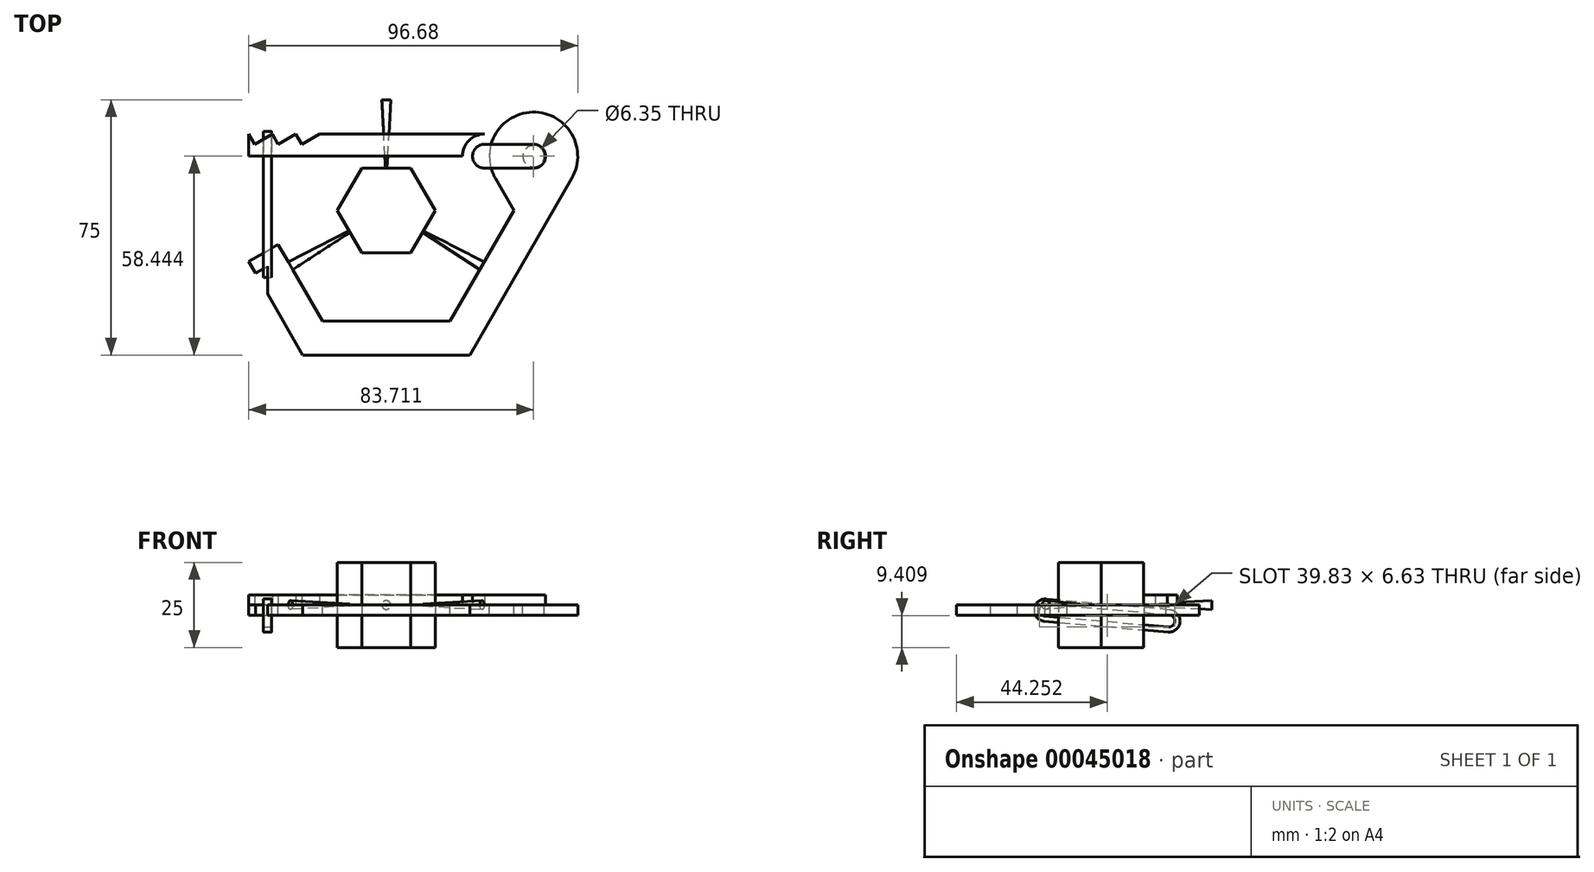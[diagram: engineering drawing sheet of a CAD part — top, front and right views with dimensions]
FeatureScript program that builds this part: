
annotation { "Feature Type Name" : "Feature", "Feature Type Description" : "" }
export const myFeature = defineFeature(function(context is Context, id is Id, definition is map)
    precondition{}
    {
        {
            var Q0;
            Q0=qCreatedBy(makeId("Top.planeOp"),FACE);
            var sketch = newSketch(context, id + "F0", { "sketchPlane" : qUnion([Q0])});
            skCircle(sketch, "E0.cCircle", {"center": v(0, 0) * mm, "radius": 12.5 * mm, "construction": true});
            skLineSegment(sketch, "E0.0", {"start": v(7.22, 12.5) * mm, "end": v(14.43, 0) * mm});
            skLineSegment(sketch, "E0.1", {"start": v(14.43, 0) * mm, "end": v(7.22, -12.5) * mm});
            skLineSegment(sketch, "E0.2", {"start": v(7.22, -12.5) * mm, "end": v(-7.22, -12.5) * mm});
            skLineSegment(sketch, "E0.3", {"start": v(-7.22, -12.5) * mm, "end": v(-14.43, 0) * mm});
            skLineSegment(sketch, "E0.4", {"start": v(-14.43, 0) * mm, "end": v(-7.22, 12.5) * mm});
            skLineSegment(sketch, "E0.5", {"start": v(-7.22, 12.5) * mm, "end": v(7.22, 12.5) * mm});
            skLineSegment(sketch, "E1.0", {"start": v(32.07, 9.46) * mm, "end": v(37.53, 0) * mm});
            skLineSegment(sketch, "E1.1", {"start": v(18.76, -32.5) * mm, "end": v(-18.76, -32.5) * mm});
            skLineSegment(sketch, "E1.2", {"start": v(-18.76, -32.5) * mm, "end": v(-31.75, -10) * mm});
            skLineSegment(sketch, "E1.3", {"start": v(37.53, 0) * mm, "end": v(18.76, -32.5) * mm});
            skLineSegment(sketch, "E2.0", {"start": v(-24.54, -42.5) * mm, "end": v(-40.41, -15) * mm});
            skLineSegment(sketch, "E2.1", {"start": v(24.54, -42.5) * mm, "end": v(-24.54, -42.5) * mm});
            skLineSegment(sketch, "E2.2", {"start": v(49.07, 0) * mm, "end": v(24.54, -42.5) * mm});
            skLineSegment(sketch, "E3", {"start": v(-40.41, -15) * mm, "end": v(-31.75, -10) * mm});
            skLineSegment(sketch, "E4", {"start": v(49.07, 0) * mm, "end": v(54.54, 9.46) * mm});
            skCircle(sketch, "E5", {"center": v(43.3, 15.94) * mm, "radius": 3.18 * mm});
            skLineSegment(sketch, "E6", {"start": v(-31.75, -10) * mm, "end": v(24.54, 22.5) * mm, "construction": true});
            skArc(sketch, "E7", {"start": v(32.07, 9.46) * mm, "mid": v(43.3, 28.92) * mm, "end": v(54.54, 9.46) * mm});
            skPoint(sketch, "E8.start.orphan", {"position": v(43.3, 33.33) * mm});
            skPoint(sketch, "E9.orphan", {"position": v(62.07, 22.5) * mm});
            skLineSegment(sketch, "E10", {"start": v(-38.41, -18.47) * mm, "end": v(-34.9, -16.44) * mm});
            skLineSegment(sketch, "E11", {"start": v(-34.9, -16.44) * mm, "end": v(-34.9, -24.55) * mm});
            skSolve(sketch);
        }
        {
            var Q0;
            Q0=qCreatedBy(makeId("Top.planeOp"),FACE);
            var sketch = newSketch(context, id + "F1", { "sketchPlane" : qUnion([Q0])});
            skLineSegment(sketch, "E12", {"start": v(43.3, 15.94) * mm, "end": v(28.87, 15.94) * mm, "construction": true});
            skArc(sketch, "E13.0.startCap", {"start": v(43.3, 19.44) * mm, "mid": v(46.8, 15.94) * mm, "end": v(43.3, 12.44) * mm});
            skArc(sketch, "E13.0.endCap", {"start": v(28.87, 12.44) * mm, "mid": v(25.37, 15.94) * mm, "end": v(28.87, 19.44) * mm});
            skLineSegment(sketch, "E13.0.left", {"start": v(43.3, 12.44) * mm, "end": v(28.87, 12.44) * mm});
            skLineSegment(sketch, "E13.0.right", {"start": v(43.3, 19.44) * mm, "end": v(28.87, 19.44) * mm});
            skLineSegment(sketch, "E14.0", {"start": v(37.82, 9.44) * mm, "end": v(28.87, 9.44) * mm});
            skLineSegment(sketch, "E14.2", {"start": v(37.82, 22.44) * mm, "end": v(28.87, 22.44) * mm});
            skArc(sketch, "E14.3", {"start": v(28.87, 9.44) * mm, "mid": v(22.37, 15.94) * mm, "end": v(28.87, 22.44) * mm});
            skLineSegment(sketch, "E15", {"start": v(28.87, 22.44) * mm, "end": v(-19.63, 22.44) * mm});
            skPoint(sketch, "E16.endSnap0", {"position": v(22.37, 15.94) * mm});
            skLineSegment(sketch, "E17", {"start": v(-40.41, 15.94) * mm, "end": v(22.37, 15.94) * mm});
            skArc(sketch, "E18", {"start": v(37.82, 22.44) * mm, "mid": v(51.8, 15.94) * mm, "end": v(37.82, 9.44) * mm});
            skLineSegment(sketch, "E19", {"start": v(-24.83, 19.44) * mm, "end": v(-19.63, 22.44) * mm});
            skLineSegment(sketch, "E20", {"start": v(-26.56, 22.44) * mm, "end": v(-24.83, 19.44) * mm});
            skLineSegment(sketch, "E21", {"start": v(-31.75, 19.44) * mm, "end": v(-26.56, 22.44) * mm});
            skLineSegment(sketch, "E22", {"start": v(-33.49, 22.44) * mm, "end": v(-31.75, 19.44) * mm});
            skLineSegment(sketch, "E23", {"start": v(-38.68, 19.44) * mm, "end": v(-33.49, 22.44) * mm});
            skLineSegment(sketch, "E24", {"start": v(-40.41, 22.44) * mm, "end": v(-38.68, 19.44) * mm});
            skLineSegment(sketch, "E25", {"start": v(-40.41, 22.44) * mm, "end": v(-40.41, 15.94) * mm});
            skSolve(sketch);
        }
        {
            var Q0;
            Q0=makeQuery(id+"F0.imprint","IMPRINT",FACE,{"disambiguationData":[TD([[makeQuery(id+"F0.imprint","IMPRINT",EDGE,{"derivedFrom":sQuery(id+"F0.wireOp",EDGE,"E1.0")}),1.0]])]});
            extrude(context, id + "F2", {"entities" : qUnion([Q0]), "oppositeDirection" : true, "depth" : 3 * mm});
        }
        {
            var Q0;
            {var subQ0=sQuery(id+"F1.wireOp",EDGE,"E15");Q0=makeQuery(id+"F1.imprint","IMPRINT",FACE,{"disambiguationData":[TD([[makeQuery(id+"F1.imprint","IMPRINT",EDGE,{"derivedFrom":subQ0}),1.0]])]});}
            var Q1;
            Q1=makeQuery(id+"F1.imprint","IMPRINT",FACE,{"disambiguationData":[TD([[makeQuery(id+"F1.imprint","IMPRINT",EDGE,{"derivedFrom":sQuery(id+"F1.wireOp",EDGE,"E13.0.startCap")}),1.0]])]});
            extrude(context, id + "F3", {"entities" : qUnion([Q0, Q1]), "depth" : 3 * mm});
        }
        {
            var Q0;
            Q0=makeQuery(id+"F0.imprint","IMPRINT",FACE,{"disambiguationData":[TD([[makeQuery(id+"F0.imprint","IMPRINT",EDGE,{"derivedFrom":sQuery(id+"F0.wireOp",EDGE,"E0.0")}),-1.0]])]});
            extrude(context, id + "F4", {"entities" : qUnion([Q0]), "endBound" : BoundingType.SYMMETRIC, "depth" : 25 * mm});
        }
        {
            var Q0;
            Q0=makeQuery(id+"F4.opExtrude","SWEPT_FACE",FACE,{"disambiguationData":[OSD([sQuery(id+"F0.wireOp",EDGE,"E0.3")])]});
            var sketch = newSketch(context, id + "F5", { "sketchPlane" : qUnion([Q0])});
            skCircle(sketch, "E26", {"center": v(0, 0) * mm, "radius": 0.25 * mm});
            skSolve(sketch);
        }
        {
            var Q0;
            Q0=makeQuery(id+"F5.imprint","IMPRINT",FACE,{"disambiguationData":[TD([[makeQuery(id+"F5.imprint","IMPRINT",EDGE,{"derivedFrom":sQuery(id+"F5.wireOp",EDGE,"E26")}),1.0]])]});
            var Q1;
            Q1=makeQuery(id+"F2.opExtrude","SWEPT_FACE",FACE,{"disambiguationData":[OSD([sQuery(id+"F0.wireOp",EDGE,"E1.2")])]});
            extrude(context, id + "F6", {"entities" : qUnion([Q0]), "endBound" : BoundingType.UP_TO_SURFACE, "endBoundEntityFace" : qUnion([Q1]), "depth" : 25 * mm, "hasDraft" : true, "draftAngle" : 3 * degree});
        }
        {
            var Q0;
            Q0=makeQuery(id+"F6.opExtrude","SWEPT_BODY",BODY,{"disambiguationData":[OSD([sQuery(id+"F5.wireOp",EDGE,"E26")])]});
            var Q1;
            Q1=sQuery(id+"F0.wireOp",EDGE,"E0.cCircle");
            circularPattern(context, id + "F7", {"entities" : qUnion([Q0]), "axis" : qUnion([Q1]), "angle" : 120 * degree, "instanceCount" : 3});
        }
        {
            var Q0;
            Q0=makeQuery(id+"F2.opExtrude","SWEPT_FACE",FACE,{"disambiguationData":[OSD([sQuery(id+"F0.wireOp",EDGE,"E11")])]});
            var sketch = newSketch(context, id + "F8", { "sketchPlane" : qUnion([Q0])});
            skLineSegment(sketch, "E27", {"start": v(16.44, -1.5) * mm, "end": v(-20.08, -1.5) * mm, "construction": true});
            skArc(sketch, "E28.0.startCap", {"start": v(16.44, 1) * mm, "mid": v(18.94, -1.5) * mm, "end": v(16.44, -4) * mm});
            skArc(sketch, "E28.0.endCap", {"start": v(-20.08, -4) * mm, "mid": v(-22.58, -1.5) * mm, "end": v(-20.08, 1) * mm});
            skLineSegment(sketch, "E28.0.left", {"start": v(16.44, -4) * mm, "end": v(-20.08, -4) * mm});
            skLineSegment(sketch, "E28.0.right", {"start": v(16.44, 1) * mm, "end": v(-20.08, 1) * mm});
            skSolve(sketch);
        }
        {
            var Q0;
            Q0=sQuery(id+"F8.wireOp",EDGE,"E28.0.left");
            var Q1;
            Q1=sQuery(id+"F8.wireOp",VERTEX,"E28.0.left.start");
            cPlane(context, id + "F9", {"entities" : qUnion([Q0, Q1]), "cplaneType" : CPlaneType.LINE_POINT, "offset" : 150 * mm, "width" : 150 * mm, "height" : 150 * mm});
        }
        {
            var Q0;
            Q0=qCreatedBy(id+"F9.planeOp",FACE);
            var sketch = newSketch(context, id + "F10", { "sketchPlane" : qUnion([Q0])});
            skLineSegment(sketch, "E29.rect.bottom", {"start": v(36.12, -3.23) * mm, "end": v(33.68, -3.23) * mm});
            skLineSegment(sketch, "E29.rect.top", {"start": v(36.12, -4.77) * mm, "end": v(33.68, -4.77) * mm});
            skLineSegment(sketch, "E29.rect.left", {"start": v(36.12, -3.23) * mm, "end": v(36.12, -4.77) * mm});
            skLineSegment(sketch, "E29.rect.right", {"start": v(33.68, -3.23) * mm, "end": v(33.68, -4.77) * mm});
            skPoint(sketch, "E29.rect.middle", {"position": v(34.9, -4) * mm});
            skSolve(sketch);
        }
        {
            var Q0;
            Q0=makeQuery(id+"F10.imprint","IMPRINT",FACE,{"disambiguationData":[TD([[makeQuery(id+"F10.imprint","IMPRINT",EDGE,{"derivedFrom":sQuery(id+"F10.wireOp",EDGE,"E29.rect.bottom")}),1.0]])]});
            var Q1;
            Q1=sQuery(id+"F8.wireOp",EDGE,"E28.0.left");
            var Q2;
            Q2=sQuery(id+"F8.wireOp",EDGE,"E28.0.endCap");
            var Q3;
            Q3=sQuery(id+"F8.wireOp",EDGE,"E28.0.right");
            var Q4;
            Q4=sQuery(id+"F8.wireOp",EDGE,"E28.0.startCap");
            sweep(context, id + "F11", {"profiles" : qUnion([Q0]), "path" : qUnion([Q1, Q2, Q3, Q4])});
        }
        {
            var Q0;
            Q0=makeQuery(id+"F11.opSweep","SWEPT_BODY",BODY,{"disambiguationData":[OSD([sQuery(id+"F8.wireOp",EDGE,"E28.0.startCap"),sQuery(id+"F10.wireOp",EDGE,"E29.rect.bottom"),sQuery(id+"F10.wireOp",EDGE,"E29.rect.top"),sQuery(id+"F10.wireOp",EDGE,"E29.rect.left"),sQuery(id+"F10.wireOp",EDGE,"E29.rect.right")])]});
            var Q1;
            Q1=makeQuery(id+"F11.opSweep","SWEPT_FACE",FACE,{"disambiguationData":[OSD([sQuery(id+"F8.wireOp",EDGE,"E28.0.startCap"),sQuery(id+"F10.wireOp",EDGE,"E29.rect.top")])]});
            transform(context, id + "F12", {"entities" : qUnion([Q0]), "transformType" : TransformType.ROTATION, "transformAxis" : qUnion([Q1]), "angle" : 5 * degree, "oppositeDirection" : true, "makeCopy" : false});
        }
    });
